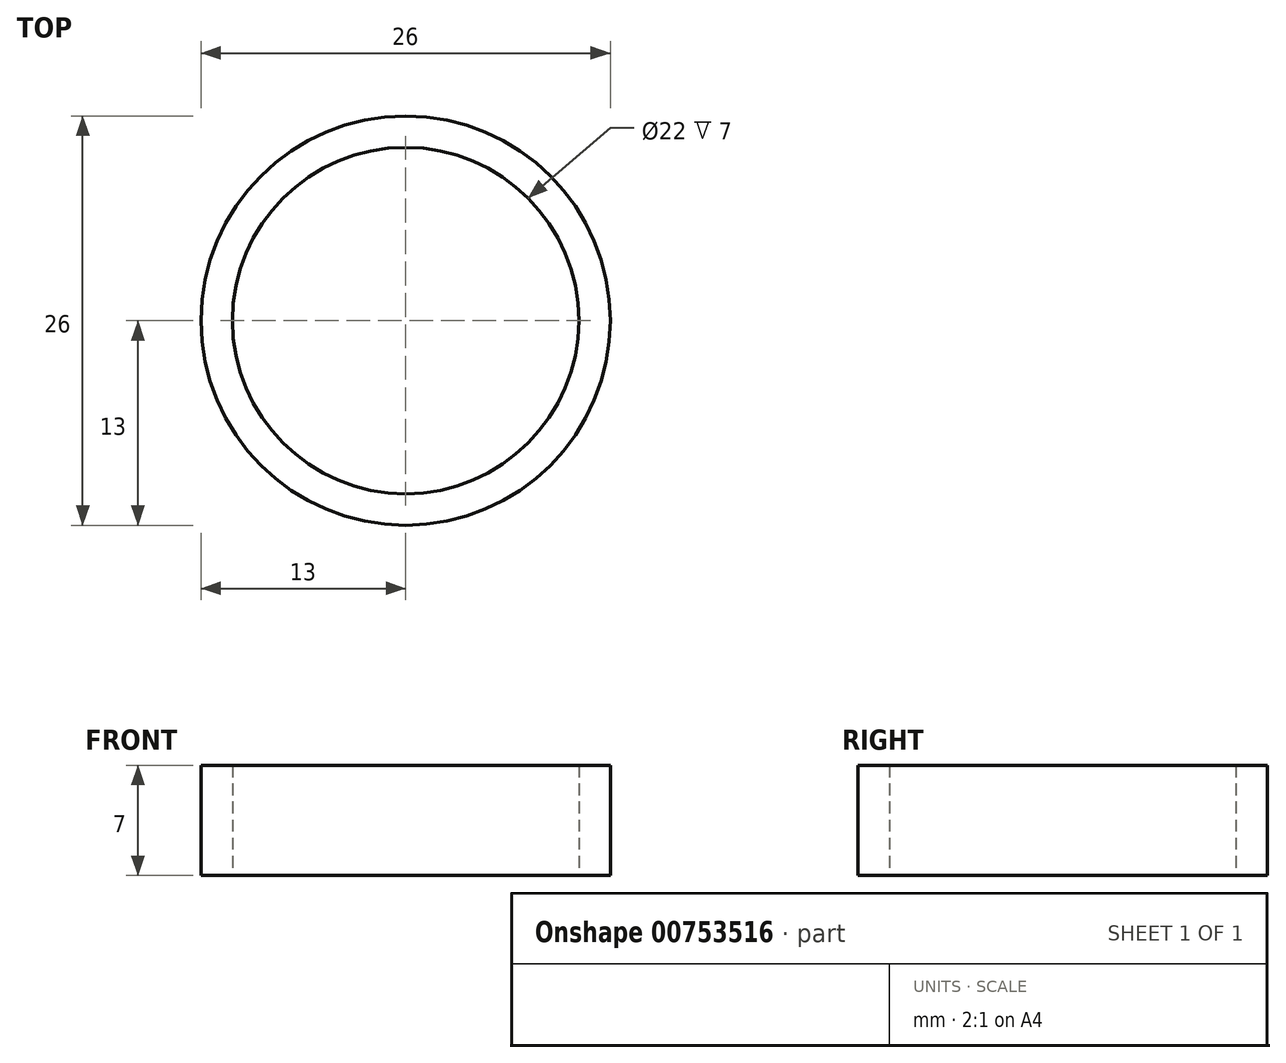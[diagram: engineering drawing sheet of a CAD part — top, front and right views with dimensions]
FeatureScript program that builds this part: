
annotation { "Feature Type Name" : "Feature", "Feature Type Description" : "" }
export const myFeature = defineFeature(function(context is Context, id is Id, definition is map)
    precondition{}
    {
        {
            var Q0;
            Q0=qCreatedBy(makeId("Top.planeOp"),FACE);
            var sketch = newSketch(context, id + "F0", { "sketchPlane" : qUnion([Q0])});
            skPoint(sketch, "E0", {"position": v(0, 0) * mm});
            skCircle(sketch, "E1", {"center": v(0, 0) * mm, "radius": 13 * mm});
            skCircle(sketch, "E2", {"center": v(0, 0) * mm, "radius": 11 * mm});
            skCircle(sketch, "E3", {"center": v(0, 22.52) * mm, "radius": 9.53 * mm});
            skCircle(sketch, "E4.cCircle", {"center": v(0, 22.52) * mm, "radius": 9.52 * mm, "construction": true});
            skLineSegment(sketch, "E4.0", {"start": v(5.5, 13) * mm, "end": v(-5.5, 13) * mm});
            skLineSegment(sketch, "E4.1", {"start": v(-5.5, 13) * mm, "end": v(-11, 22.52) * mm});
            skLineSegment(sketch, "E4.2", {"start": v(-11, 22.52) * mm, "end": v(-5.5, 32.05) * mm});
            skLineSegment(sketch, "E4.3", {"start": v(-5.5, 32.05) * mm, "end": v(5.5, 32.05) * mm});
            skLineSegment(sketch, "E4.4", {"start": v(5.5, 32.05) * mm, "end": v(11, 22.53) * mm});
            skLineSegment(sketch, "E4.5", {"start": v(11, 22.52) * mm, "end": v(5.5, 13) * mm});
            skPoint(sketch, "E4.0.midPoint", {"position": v(0, 13) * mm});
            skFitSpline(sketch, "E5", {"points": [v(11.31, 6.4) * mm, v(10.83, 7.45) * mm, v(9.87, 9.52) * mm, v(9.1, 13.2) * mm, v(11, 17.4) * mm, v(15.94, 20.3) * mm, v(22.74, 19.12) * mm, v(27.23, 17.53) * mm, v(29.74, 16.64) * mm]});
            skFitSpline(sketch, "E6", {"points": [v(29.75, 16.62) * mm, v(28.49, 18.24) * mm, v(25.6, 21.94) * mm, v(20.2, 27.5) * mm, v(15.04, 28.67) * mm, v(12.57, 31.94) * mm, v(14.68, 32.45) * mm, v(15.7, 31.92) * mm, v(16.4, 31.56) * mm]});
            skFitSpline(sketch, "E7", {"points": [v(16.41, 31.55) * mm, v(15.4, 32.34) * mm, v(13.47, 33.85) * mm, v(10.35, 34.34) * mm, v(7.93, 34.4) * mm, v(6.21, 34.7) * mm, v(4.5, 35.07) * mm, v(3.1, 34.86) * mm, v(1.34, 35.88) * mm, v(3.5, 37.39) * mm, v(4.79, 36.78) * mm, v(5.65, 36.38) * mm]});
            skFitSpline(sketch, "E8", {"points": [v(5.65, 36.38) * mm, v(5.32, 36.67) * mm, v(4.7, 37.21) * mm, v(3.55, 37.65) * mm, v(2.8, 37.68) * mm, v(2.42, 37.7) * mm]});
            skFitSpline(sketch, "E9", {"points": [v(2.42, 37.7) * mm, v(1.45, 37.5) * mm, v(-0.48, 37.12) * mm, v(-2.75, 35.7) * mm, v(-4.67, 34.66) * mm, v(-6.3, 34.24) * mm, v(-7.7, 33.6) * mm, v(-8.64, 32.83) * mm, v(-10.18, 32.32) * mm, v(-10.18, 34.32) * mm, v(-9.04, 34.75) * mm, v(-8.22, 35.06) * mm]});
            skFitSpline(sketch, "E10", {"points": [v(-8.19, 35.07) * mm, v(-9.62, 34.73) * mm, v(-12.04, 34.16) * mm, v(-12.7, 30.8) * mm, v(-12.62, 28.55) * mm, v(-13.26, 26.7) * mm, v(-13.46, 25) * mm, v(-13.67, 21.66) * mm, v(-12.51, 16.97) * mm, v(-8.77, 13.8) * mm, v(-7.89, 11.37) * mm, v(-7.6, 10.55) * mm]});
            skLineSegment(sketch, "E11", {"start": v(-5.77, 15.6) * mm, "end": v(-5.77, 15.6) * mm});
            skSolve(sketch);
        }
        {
            var Q0;
            {var subQ17=sQuery(id+"F0.wireOp",EDGE,"f13e69a9-4a04-4aee-8a80-34e2075970d7");Q0=makeQuery(id+"F0.imprint","IMPRINT",FACE,{"disambiguationData":[TD([[makeQuery(id+"F0.imprint","IMPRINT",EDGE,{"derivedFrom":subQ17}),-1.0]])]});}
            var Q1;
            Q1=makeQuery(id+"F0.imprint","IMPRINT",FACE,{"disambiguationData":[TD([[makeQuery(id+"F0.imprint","IMPRINT",EDGE,{"derivedFrom":sQuery(id+"F0.wireOp",EDGE,"E2")}),-1.0]])]});
            var Q2;
            {var subQ18=sQuery(id+"F0.wireOp",EDGE,"E5");Q2=makeQuery(id+"F0.imprint","IMPRINT",FACE,{"disambiguationData":[TD([[makeQuery(id+"F0.imprint","IMPRINT",EDGE,{"derivedFrom":subQ18}),1.0]])]});}
            extrude(context, id + "F1", {"entities" : qUnion([Q0, Q1, Q2]), "depth" : 7 * mm, "offsetDistance" : 25 * mm});
        }
        {
            var Q0;
            Q0=makeQuery(id+"F1.opExtrude","SWEPT_BODY",BODY,{"disambiguationData":[OSD([sQuery(id+"F0.wireOp",EDGE,"E1"),sQuery(id+"F0.wireOp",EDGE,"E2"),sQuery(id+"F0.wireOp",EDGE,"E4.0"),sQuery(id+"F0.wireOp",EDGE,"E4.1"),sQuery(id+"F0.wireOp",EDGE,"E4.2"),sQuery(id+"F0.wireOp",EDGE,"E4.3"),sQuery(id+"F0.wireOp",EDGE,"E4.4"),sQuery(id+"F0.wireOp",EDGE,"E4.5"),sQuery(id+"F0.wireOp",EDGE,"f13e69a9-4a04-4aee-8a80-34e2075970d7"),sQuery(id+"F0.wireOp",EDGE,"befc780b-96c6-47c0-ab00-88d7bbef90b9")])]});
            var Q1;
            Q1=makeQuery(id+"F1.opExtrude","CAP_EDGE",EDGE,{"disambiguationData":[OSD([sQuery(id+"F0.wireOp",EDGE,"E2")])],"isStart":false});
            circularPattern(context, id + "F2", {"operationType" : NewBodyOperationType.ADD, "entities" : qUnion([Q0]), "axis" : qUnion([Q1]), "angle" : 360 * degree, "instanceCount" : 3, "equalSpace" : true});
        }
    });
